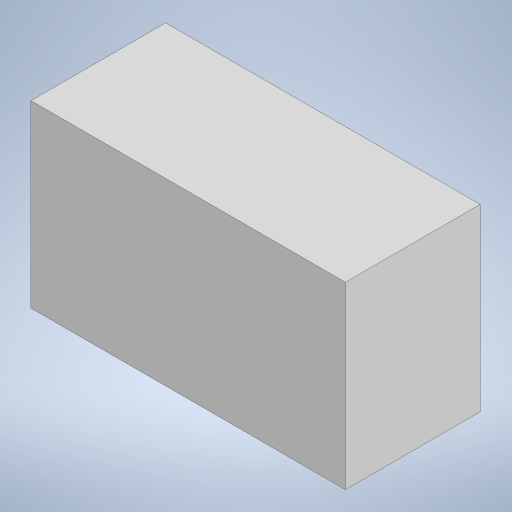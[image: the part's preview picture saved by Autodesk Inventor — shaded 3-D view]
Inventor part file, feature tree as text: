
AUTODESK INVENTOR PART (.ipt)
format: ipt  version: 2024.3 (Build 283343000, 343)  size: 173,056 bytes
history: native  units: mm
features: extrude x2, sketch x2, other x1
ambient origin geometry x8: Origin, YZ Plane, XZ Plane, XY Plane, X Axis, Y Axis, Z Axis, Center Point
bodies: Body1 (feature_tree)
feature tree (5):
  other  "ソリッド1"
  extrude  "押し出し1"  Depth=350.0mm
  extrude  "押し出し2"  Depth=200.0mm
  sketch  "スケッチ1"
  sketch  "スケッチ2"
